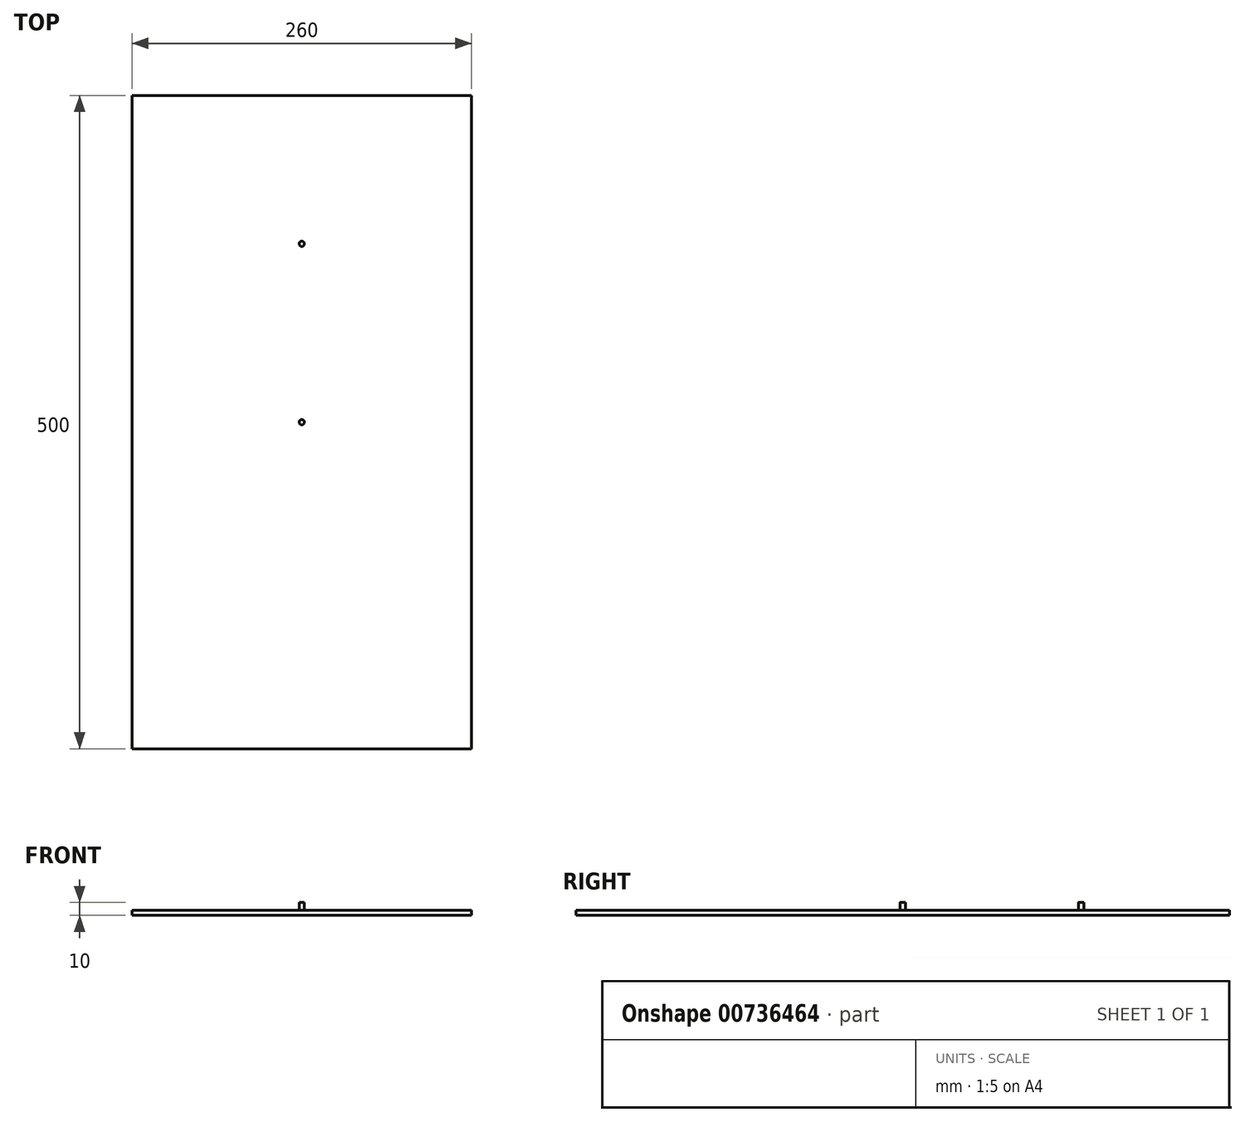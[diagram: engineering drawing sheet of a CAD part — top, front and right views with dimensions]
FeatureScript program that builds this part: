
annotation { "Feature Type Name" : "Feature", "Feature Type Description" : "" }
export const myFeature = defineFeature(function(context is Context, id is Id, definition is map)
    precondition{}
    {
        {
            var Q0;
            Q0=qCreatedBy(makeId("Top.planeOp"),FACE);
            var sketch = newSketch(context, id + "F0", { "sketchPlane" : qUnion([Q0])});
            skLineSegment(sketch, "E0.bottom", {"start": v(130, 250) * mm, "end": v(-130, 250) * mm});
            skLineSegment(sketch, "E0.top", {"start": v(130, -250) * mm, "end": v(-130, -250) * mm});
            skLineSegment(sketch, "E0.left", {"start": v(130, 250) * mm, "end": v(130, -250) * mm});
            skLineSegment(sketch, "E0.right", {"start": v(-130, 250) * mm, "end": v(-130, -250) * mm});
            skPoint(sketch, "E0.middle", {"position": v(0, 0) * mm});
            skSolve(sketch);
        }
        {
            var Q0;
            Q0 = qSketchRegion(id + "F0", true);
            extrude(context, id + "F1", {"entities" : qUnion([Q0]), "oppositeDirection" : true, "depth" : 4 * mm, "offsetDistance" : 25 * mm});
        }
        {
            var Q0;
            Q0=makeQuery(id+"F1.opExtrude","CAP_FACE",FACE,{"disambiguationData":[OSD([sQuery(id+"F0.wireOp",EDGE,"E0.bottom"),sQuery(id+"F0.wireOp",EDGE,"E0.top"),sQuery(id+"F0.wireOp",EDGE,"E0.left"),sQuery(id+"F0.wireOp",EDGE,"E0.right")])],"isStart":true});
            var sketch = newSketch(context, id + "F2", { "sketchPlane" : qUnion([Q0])});
            skCircle(sketch, "E1", {"center": v(0, 0) * mm, "radius": 2 * mm});
            skCircle(sketch, "E2", {"center": v(0, 136.5) * mm, "radius": 2 * mm});
            skSolve(sketch);
        }
        {
            var Q0;
            Q0 = qSketchRegion(id + "F2", true);
            extrude(context, id + "F3", {"entities" : qUnion([Q0]), "operationType" : NewBodyOperationType.ADD, "depth" : 6 * mm, "offsetDistance" : 25 * mm});
        }
    });
